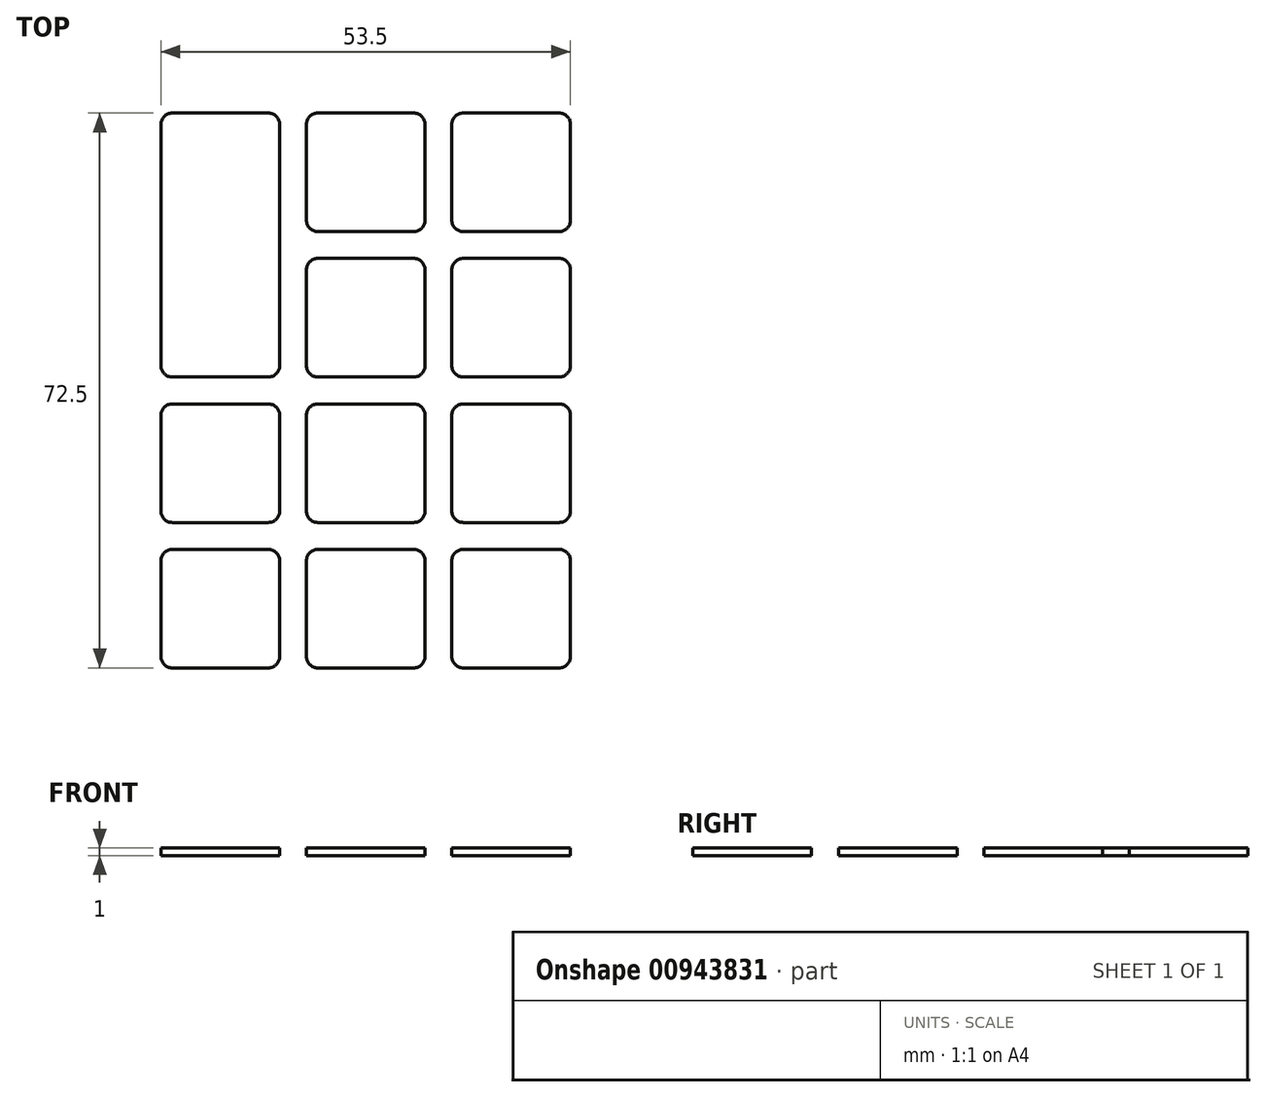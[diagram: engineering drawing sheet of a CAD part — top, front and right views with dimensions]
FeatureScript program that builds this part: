
annotation { "Feature Type Name" : "Feature", "Feature Type Description" : "" }
export const myFeature = defineFeature(function(context is Context, id is Id, definition is map)
    precondition{}
    {
        {
            var Q0;
            Q0=qCreatedBy(makeId("Top.planeOp"),FACE);
            var sketch = newSketch(context, id + "F0", { "sketchPlane" : qUnion([Q0])});
            skLineSegment(sketch, "E0.bottom", {"start": v(0, 0) * mm, "end": v(19, 0) * mm, "construction": true});
            skLineSegment(sketch, "E0.top", {"start": v(0, 19) * mm, "end": v(19, 19) * mm, "construction": true});
            skLineSegment(sketch, "E0.left", {"start": v(0, 0) * mm, "end": v(0, 19) * mm, "construction": true});
            skLineSegment(sketch, "E0.right", {"start": v(19, 0) * mm, "end": v(19, 19) * mm, "construction": true});
            skLineSegment(sketch, "E1.bottom", {"start": v(3.25, 17.25) * mm, "end": v(15.75, 17.25) * mm});
            skLineSegment(sketch, "E1.top", {"start": v(3.25, 1.75) * mm, "end": v(15.75, 1.75) * mm});
            skLineSegment(sketch, "E1.left", {"start": v(1.75, 15.75) * mm, "end": v(1.75, 3.25) * mm});
            skLineSegment(sketch, "E1.right", {"start": v(17.25, 15.75) * mm, "end": v(17.25, 3.25) * mm});
            skPoint(sketch, "E2.visualSharp", {"position": v(1.75, 17.25) * mm});
            skArc(sketch, "E2.filletArc", {"start": v(3.25, 17.25) * mm, "mid": v(2.19, 16.81) * mm, "end": v(1.75, 15.75) * mm});
            skPoint(sketch, "E3.visualSharp", {"position": v(17.25, 17.25) * mm});
            skArc(sketch, "E3.filletArc", {"start": v(17.25, 15.75) * mm, "mid": v(16.81, 16.81) * mm, "end": v(15.75, 17.25) * mm});
            skPoint(sketch, "E4.visualSharp", {"position": v(17.25, 1.75) * mm});
            skArc(sketch, "E4.filletArc", {"start": v(15.75, 1.75) * mm, "mid": v(16.81, 2.19) * mm, "end": v(17.25, 3.25) * mm});
            skPoint(sketch, "E5.visualSharp", {"position": v(1.75, 1.75) * mm});
            skArc(sketch, "E5.filletArc", {"start": v(1.75, 3.25) * mm, "mid": v(2.19, 2.19) * mm, "end": v(3.25, 1.75) * mm});
            skArc(sketch, "E6.0.1.0", {"start": v(17.25, 34.75) * mm, "mid": v(16.81, 35.81) * mm, "end": v(15.75, 36.25) * mm});
            skPoint(sketch, "E6.0.1.1", {"position": v(17.25, 36.25) * mm});
            skArc(sketch, "E6.0.1.2", {"start": v(15.75, 20.75) * mm, "mid": v(16.81, 21.19) * mm, "end": v(17.25, 22.25) * mm});
            skLineSegment(sketch, "E6.0.1.3", {"start": v(3.25, 36.25) * mm, "end": v(15.75, 36.25) * mm});
            skLineSegment(sketch, "E6.0.1.4", {"start": v(17.25, 34.75) * mm, "end": v(17.25, 22.25) * mm});
            skPoint(sketch, "E6.0.1.5", {"position": v(1.75, 20.75) * mm});
            skArc(sketch, "E6.0.1.6", {"start": v(3.25, 36.25) * mm, "mid": v(2.19, 35.81) * mm, "end": v(1.75, 34.75) * mm});
            skPoint(sketch, "E6.0.1.7", {"position": v(17.25, 20.75) * mm});
            skArc(sketch, "E6.0.1.8", {"start": v(1.75, 22.25) * mm, "mid": v(2.19, 21.19) * mm, "end": v(3.25, 20.75) * mm});
            skLineSegment(sketch, "E6.0.1.9", {"start": v(1.75, 34.75) * mm, "end": v(1.75, 22.25) * mm});
            skLineSegment(sketch, "E6.0.1.10", {"start": v(3.25, 20.75) * mm, "end": v(15.75, 20.75) * mm});
            skPoint(sketch, "E6.0.1.11", {"position": v(1.75, 36.25) * mm});
            skPoint(sketch, "E6.0.2.1", {"position": v(17.25, 55.25) * mm});
            skArc(sketch, "E6.0.2.2", {"start": v(15.75, 39.75) * mm, "mid": v(16.81, 40.19) * mm, "end": v(17.25, 41.25) * mm});
            skLineSegment(sketch, "E6.0.2.4", {"start": v(17.25, 53.75) * mm, "end": v(17.25, 41.25) * mm});
            skPoint(sketch, "E6.0.2.5", {"position": v(1.75, 39.75) * mm});
            skPoint(sketch, "E6.0.2.7", {"position": v(17.25, 39.75) * mm});
            skArc(sketch, "E6.0.2.8", {"start": v(1.75, 41.25) * mm, "mid": v(2.19, 40.19) * mm, "end": v(3.25, 39.75) * mm});
            skLineSegment(sketch, "E6.0.2.9", {"start": v(1.75, 53.75) * mm, "end": v(1.75, 41.25) * mm});
            skLineSegment(sketch, "E6.0.2.10", {"start": v(3.25, 39.75) * mm, "end": v(15.75, 39.75) * mm});
            skPoint(sketch, "E6.0.2.11", {"position": v(1.75, 55.25) * mm});
            skArc(sketch, "E6.0.3.0", {"start": v(17.25, 72.75) * mm, "mid": v(16.81, 73.81) * mm, "end": v(15.75, 74.25) * mm});
            skPoint(sketch, "E6.0.3.1", {"position": v(17.25, 74.25) * mm});
            skLineSegment(sketch, "E6.0.3.3", {"start": v(3.25, 74.25) * mm, "end": v(15.75, 74.25) * mm});
            skLineSegment(sketch, "E6.0.3.4", {"start": v(17.25, 72.75) * mm, "end": v(17.25, 60.25) * mm});
            skPoint(sketch, "E6.0.3.5", {"position": v(1.75, 58.75) * mm});
            skArc(sketch, "E6.0.3.6", {"start": v(3.25, 74.25) * mm, "mid": v(2.19, 73.81) * mm, "end": v(1.75, 72.75) * mm});
            skPoint(sketch, "E6.0.3.7", {"position": v(17.25, 58.75) * mm});
            skLineSegment(sketch, "E6.0.3.9", {"start": v(1.75, 72.75) * mm, "end": v(1.75, 60.25) * mm});
            skPoint(sketch, "E6.0.3.11", {"position": v(1.75, 74.25) * mm});
            skArc(sketch, "E6.1.0.0", {"start": v(36.25, 15.75) * mm, "mid": v(35.81, 16.81) * mm, "end": v(34.75, 17.25) * mm});
            skPoint(sketch, "E6.1.0.1", {"position": v(36.25, 17.25) * mm});
            skArc(sketch, "E6.1.0.2", {"start": v(34.75, 1.75) * mm, "mid": v(35.81, 2.19) * mm, "end": v(36.25, 3.25) * mm});
            skLineSegment(sketch, "E6.1.0.3", {"start": v(22.25, 17.25) * mm, "end": v(34.75, 17.25) * mm});
            skLineSegment(sketch, "E6.1.0.4", {"start": v(36.25, 15.75) * mm, "end": v(36.25, 3.25) * mm});
            skPoint(sketch, "E6.1.0.5", {"position": v(20.75, 1.75) * mm});
            skArc(sketch, "E6.1.0.6", {"start": v(22.25, 17.25) * mm, "mid": v(21.19, 16.81) * mm, "end": v(20.75, 15.75) * mm});
            skPoint(sketch, "E6.1.0.7", {"position": v(36.25, 1.75) * mm});
            skArc(sketch, "E6.1.0.8", {"start": v(20.75, 3.25) * mm, "mid": v(21.19, 2.19) * mm, "end": v(22.25, 1.75) * mm});
            skLineSegment(sketch, "E6.1.0.9", {"start": v(20.75, 15.75) * mm, "end": v(20.75, 3.25) * mm});
            skLineSegment(sketch, "E6.1.0.10", {"start": v(22.25, 1.75) * mm, "end": v(34.75, 1.75) * mm});
            skPoint(sketch, "E6.1.0.11", {"position": v(20.75, 17.25) * mm});
            skArc(sketch, "E6.1.1.0", {"start": v(36.25, 34.75) * mm, "mid": v(35.81, 35.81) * mm, "end": v(34.75, 36.25) * mm});
            skPoint(sketch, "E6.1.1.1", {"position": v(36.25, 36.25) * mm});
            skArc(sketch, "E6.1.1.2", {"start": v(34.75, 20.75) * mm, "mid": v(35.81, 21.19) * mm, "end": v(36.25, 22.25) * mm});
            skLineSegment(sketch, "E6.1.1.3", {"start": v(22.25, 36.25) * mm, "end": v(34.75, 36.25) * mm});
            skLineSegment(sketch, "E6.1.1.4", {"start": v(36.25, 34.75) * mm, "end": v(36.25, 22.25) * mm});
            skPoint(sketch, "E6.1.1.5", {"position": v(20.75, 20.75) * mm});
            skArc(sketch, "E6.1.1.6", {"start": v(22.25, 36.25) * mm, "mid": v(21.19, 35.81) * mm, "end": v(20.75, 34.75) * mm});
            skPoint(sketch, "E6.1.1.7", {"position": v(36.25, 20.75) * mm});
            skArc(sketch, "E6.1.1.8", {"start": v(20.75, 22.25) * mm, "mid": v(21.19, 21.19) * mm, "end": v(22.25, 20.75) * mm});
            skLineSegment(sketch, "E6.1.1.9", {"start": v(20.75, 34.75) * mm, "end": v(20.75, 22.25) * mm});
            skLineSegment(sketch, "E6.1.1.10", {"start": v(22.25, 20.75) * mm, "end": v(34.75, 20.75) * mm});
            skPoint(sketch, "E6.1.1.11", {"position": v(20.75, 36.25) * mm});
            skArc(sketch, "E6.1.2.0", {"start": v(36.25, 53.75) * mm, "mid": v(35.81, 54.81) * mm, "end": v(34.75, 55.25) * mm});
            skPoint(sketch, "E6.1.2.1", {"position": v(36.25, 55.25) * mm});
            skArc(sketch, "E6.1.2.2", {"start": v(34.75, 39.75) * mm, "mid": v(35.81, 40.19) * mm, "end": v(36.25, 41.25) * mm});
            skLineSegment(sketch, "E6.1.2.3", {"start": v(22.25, 55.25) * mm, "end": v(34.75, 55.25) * mm});
            skLineSegment(sketch, "E6.1.2.4", {"start": v(36.25, 53.75) * mm, "end": v(36.25, 41.25) * mm});
            skPoint(sketch, "E6.1.2.5", {"position": v(20.75, 39.75) * mm});
            skArc(sketch, "E6.1.2.6", {"start": v(22.25, 55.25) * mm, "mid": v(21.19, 54.81) * mm, "end": v(20.75, 53.75) * mm});
            skPoint(sketch, "E6.1.2.7", {"position": v(36.25, 39.75) * mm});
            skArc(sketch, "E6.1.2.8", {"start": v(20.75, 41.25) * mm, "mid": v(21.19, 40.19) * mm, "end": v(22.25, 39.75) * mm});
            skLineSegment(sketch, "E6.1.2.9", {"start": v(20.75, 53.75) * mm, "end": v(20.75, 41.25) * mm});
            skLineSegment(sketch, "E6.1.2.10", {"start": v(22.25, 39.75) * mm, "end": v(34.75, 39.75) * mm});
            skPoint(sketch, "E6.1.2.11", {"position": v(20.75, 55.25) * mm});
            skArc(sketch, "E6.1.3.0", {"start": v(36.25, 72.75) * mm, "mid": v(35.81, 73.81) * mm, "end": v(34.75, 74.25) * mm});
            skPoint(sketch, "E6.1.3.1", {"position": v(36.25, 74.25) * mm});
            skArc(sketch, "E6.1.3.2", {"start": v(34.75, 58.75) * mm, "mid": v(35.81, 59.19) * mm, "end": v(36.25, 60.25) * mm});
            skLineSegment(sketch, "E6.1.3.3", {"start": v(22.25, 74.25) * mm, "end": v(34.75, 74.25) * mm});
            skLineSegment(sketch, "E6.1.3.4", {"start": v(36.25, 72.75) * mm, "end": v(36.25, 60.25) * mm});
            skPoint(sketch, "E6.1.3.5", {"position": v(20.75, 58.75) * mm});
            skArc(sketch, "E6.1.3.6", {"start": v(22.25, 74.25) * mm, "mid": v(21.19, 73.81) * mm, "end": v(20.75, 72.75) * mm});
            skPoint(sketch, "E6.1.3.7", {"position": v(36.25, 58.75) * mm});
            skArc(sketch, "E6.1.3.8", {"start": v(20.75, 60.25) * mm, "mid": v(21.19, 59.19) * mm, "end": v(22.25, 58.75) * mm});
            skLineSegment(sketch, "E6.1.3.9", {"start": v(20.75, 72.75) * mm, "end": v(20.75, 60.25) * mm});
            skLineSegment(sketch, "E6.1.3.10", {"start": v(22.25, 58.75) * mm, "end": v(34.75, 58.75) * mm});
            skPoint(sketch, "E6.1.3.11", {"position": v(20.75, 74.25) * mm});
            skArc(sketch, "E6.2.0.0", {"start": v(55.25, 15.75) * mm, "mid": v(54.81, 16.81) * mm, "end": v(53.75, 17.25) * mm});
            skPoint(sketch, "E6.2.0.1", {"position": v(55.25, 17.25) * mm});
            skArc(sketch, "E6.2.0.2", {"start": v(53.75, 1.75) * mm, "mid": v(54.81, 2.19) * mm, "end": v(55.25, 3.25) * mm});
            skLineSegment(sketch, "E6.2.0.3", {"start": v(41.25, 17.25) * mm, "end": v(53.75, 17.25) * mm});
            skLineSegment(sketch, "E6.2.0.4", {"start": v(55.25, 15.75) * mm, "end": v(55.25, 3.25) * mm});
            skPoint(sketch, "E6.2.0.5", {"position": v(39.75, 1.75) * mm});
            skArc(sketch, "E6.2.0.6", {"start": v(41.25, 17.25) * mm, "mid": v(40.19, 16.81) * mm, "end": v(39.75, 15.75) * mm});
            skPoint(sketch, "E6.2.0.7", {"position": v(55.25, 1.75) * mm});
            skArc(sketch, "E6.2.0.8", {"start": v(39.75, 3.25) * mm, "mid": v(40.19, 2.19) * mm, "end": v(41.25, 1.75) * mm});
            skLineSegment(sketch, "E6.2.0.9", {"start": v(39.75, 15.75) * mm, "end": v(39.75, 3.25) * mm});
            skLineSegment(sketch, "E6.2.0.10", {"start": v(41.25, 1.75) * mm, "end": v(53.75, 1.75) * mm});
            skPoint(sketch, "E6.2.0.11", {"position": v(39.75, 17.25) * mm});
            skArc(sketch, "E6.2.1.0", {"start": v(55.25, 34.75) * mm, "mid": v(54.81, 35.81) * mm, "end": v(53.75, 36.25) * mm});
            skPoint(sketch, "E6.2.1.1", {"position": v(55.25, 36.25) * mm});
            skArc(sketch, "E6.2.1.2", {"start": v(53.75, 20.75) * mm, "mid": v(54.81, 21.19) * mm, "end": v(55.25, 22.25) * mm});
            skLineSegment(sketch, "E6.2.1.3", {"start": v(41.25, 36.25) * mm, "end": v(53.75, 36.25) * mm});
            skLineSegment(sketch, "E6.2.1.4", {"start": v(55.25, 34.75) * mm, "end": v(55.25, 22.25) * mm});
            skPoint(sketch, "E6.2.1.5", {"position": v(39.75, 20.75) * mm});
            skArc(sketch, "E6.2.1.6", {"start": v(41.25, 36.25) * mm, "mid": v(40.19, 35.81) * mm, "end": v(39.75, 34.75) * mm});
            skPoint(sketch, "E6.2.1.7", {"position": v(55.25, 20.75) * mm});
            skArc(sketch, "E6.2.1.8", {"start": v(39.75, 22.25) * mm, "mid": v(40.19, 21.19) * mm, "end": v(41.25, 20.75) * mm});
            skLineSegment(sketch, "E6.2.1.9", {"start": v(39.75, 34.75) * mm, "end": v(39.75, 22.25) * mm});
            skLineSegment(sketch, "E6.2.1.10", {"start": v(41.25, 20.75) * mm, "end": v(53.75, 20.75) * mm});
            skPoint(sketch, "E6.2.1.11", {"position": v(39.75, 36.25) * mm});
            skArc(sketch, "E6.2.2.0", {"start": v(55.25, 53.75) * mm, "mid": v(54.81, 54.81) * mm, "end": v(53.75, 55.25) * mm});
            skPoint(sketch, "E6.2.2.1", {"position": v(55.25, 55.25) * mm});
            skArc(sketch, "E6.2.2.2", {"start": v(53.75, 39.75) * mm, "mid": v(54.81, 40.19) * mm, "end": v(55.25, 41.25) * mm});
            skLineSegment(sketch, "E6.2.2.3", {"start": v(41.25, 55.25) * mm, "end": v(53.75, 55.25) * mm});
            skLineSegment(sketch, "E6.2.2.4", {"start": v(55.25, 53.75) * mm, "end": v(55.25, 41.25) * mm});
            skPoint(sketch, "E6.2.2.5", {"position": v(39.75, 39.75) * mm});
            skArc(sketch, "E6.2.2.6", {"start": v(41.25, 55.25) * mm, "mid": v(40.19, 54.81) * mm, "end": v(39.75, 53.75) * mm});
            skPoint(sketch, "E6.2.2.7", {"position": v(55.25, 39.75) * mm});
            skArc(sketch, "E6.2.2.8", {"start": v(39.75, 41.25) * mm, "mid": v(40.19, 40.19) * mm, "end": v(41.25, 39.75) * mm});
            skLineSegment(sketch, "E6.2.2.9", {"start": v(39.75, 53.75) * mm, "end": v(39.75, 41.25) * mm});
            skLineSegment(sketch, "E6.2.2.10", {"start": v(41.25, 39.75) * mm, "end": v(53.75, 39.75) * mm});
            skPoint(sketch, "E6.2.2.11", {"position": v(39.75, 55.25) * mm});
            skArc(sketch, "E6.2.3.0", {"start": v(55.25, 72.75) * mm, "mid": v(54.81, 73.81) * mm, "end": v(53.75, 74.25) * mm});
            skPoint(sketch, "E6.2.3.1", {"position": v(55.25, 74.25) * mm});
            skArc(sketch, "E6.2.3.2", {"start": v(53.75, 58.75) * mm, "mid": v(54.81, 59.19) * mm, "end": v(55.25, 60.25) * mm});
            skLineSegment(sketch, "E6.2.3.3", {"start": v(41.25, 74.25) * mm, "end": v(53.75, 74.25) * mm});
            skLineSegment(sketch, "E6.2.3.4", {"start": v(55.25, 72.75) * mm, "end": v(55.25, 60.25) * mm});
            skPoint(sketch, "E6.2.3.5", {"position": v(39.75, 58.75) * mm});
            skArc(sketch, "E6.2.3.6", {"start": v(41.25, 74.25) * mm, "mid": v(40.19, 73.81) * mm, "end": v(39.75, 72.75) * mm});
            skPoint(sketch, "E6.2.3.7", {"position": v(55.25, 58.75) * mm});
            skArc(sketch, "E6.2.3.8", {"start": v(39.75, 60.25) * mm, "mid": v(40.19, 59.19) * mm, "end": v(41.25, 58.75) * mm});
            skLineSegment(sketch, "E6.2.3.9", {"start": v(39.75, 72.75) * mm, "end": v(39.75, 60.25) * mm});
            skLineSegment(sketch, "E6.2.3.10", {"start": v(41.25, 58.75) * mm, "end": v(53.75, 58.75) * mm});
            skPoint(sketch, "E6.2.3.11", {"position": v(39.75, 74.25) * mm});
            skLineSegment(sketch, "E6.direction1", {"start": v(1.75, 1.75) * mm, "end": v(20.75, 1.75) * mm, "construction": true});
            skLineSegment(sketch, "E6.direction2", {"start": v(1.75, 1.75) * mm, "end": v(1.75, 20.75) * mm, "construction": true});
            skLineSegment(sketch, "E7", {"start": v(17.25, 60.25) * mm, "end": v(17.25, 53.75) * mm});
            skLineSegment(sketch, "E8", {"start": v(1.75, 53.75) * mm, "end": v(1.75, 60.25) * mm});
            skSolve(sketch);
        }
        {
            var Q0;
            Q0 = qSketchRegion(id + "F0", true);
            extrude(context, id + "F1", {"entities" : qUnion([Q0]), "depth" : 1 * mm, "offsetDistance" : 25 * mm});
        }
    });
